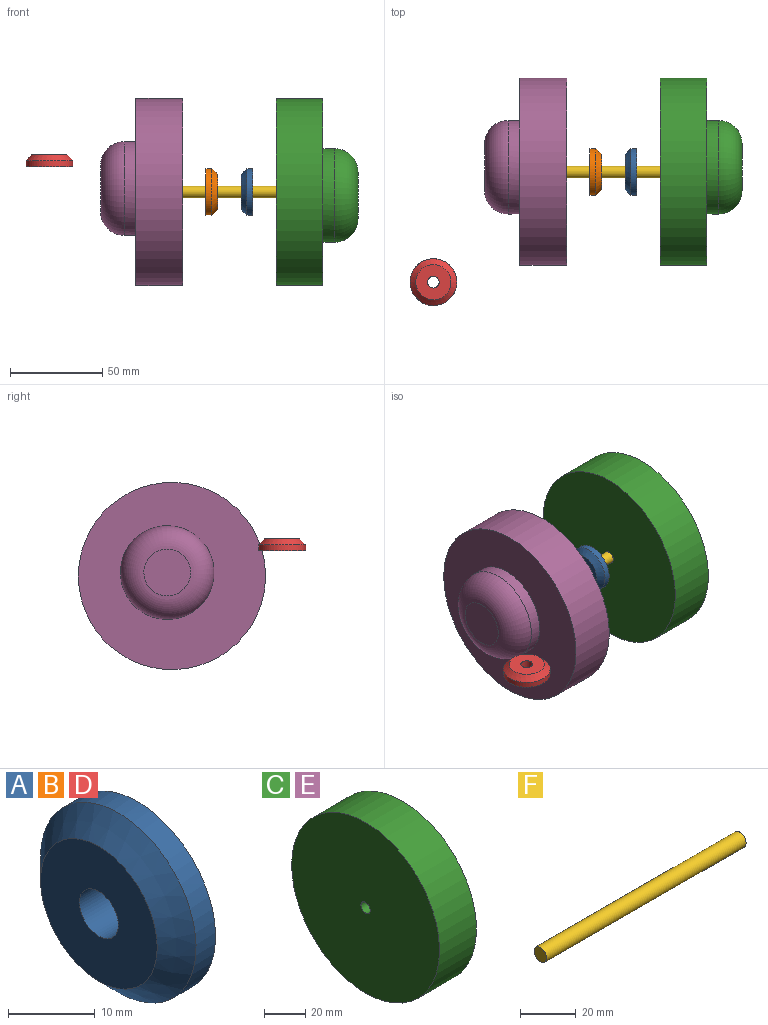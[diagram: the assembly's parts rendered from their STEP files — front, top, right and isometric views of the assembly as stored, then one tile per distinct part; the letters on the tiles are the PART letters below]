
ASSEMBLY  parts=6 mates=4
PART A: 5 faces, bbox 6.4x25.4x25.4 mm
  f0: cylinder r=12.7mm len=25.4mm, axis (1,0,0), area 253.4mm2, adj f2,f4
  f1: plane 19.05x19.05mm, normal (-1,0,0), area 253.4mm2, adj f3,f4
  f2: plane 25.4x25.4mm, normal (1,0,0), area 475mm2, adj f0,f3
  f3: cylinder r=3.17mm len=6.35mm, axis (1,0,0), area 126.7mm2, adj f1,f2
  f4: cone r=12.7mm half-angle=45deg, axis (1,0,0), area 313.5mm2, adj f0,f1
PART B: same geometry as A
PART C: 8 faces, bbox 44.5x101.6x101.6 mm
  f0: cylinder r=50.8mm len=101.6mm, axis (-1,0,0), area 8107.3mm2, adj f1,f2
  f1: plane 101.6x101.6mm, normal (1,0,0), area 6080.5mm2, adj f0,f5
  f2: plane 101.6x101.6mm, normal (-1,0,0), area 8075.7mm2, adj f0,f3
  f3: cylinder r=3.17mm len=25.4mm, axis (1,0,0), area 506.7mm2, adj f2,f6
  f4: plane 25.4x25.4mm, normal (1,0,0), area 506.7mm2, adj f7
  f5: cylinder r=25.4mm len=50.8mm, axis (-1,0,0), area 1013.4mm2, adj f1,f7
  f6: plane 6.35x6.35mm, normal (-1,0,0), area 31.7mm2, adj f3
  f7: torus R=12.7mm, axis (1,0,0), area 2605.3mm2, adj f4,f5
PART D: same geometry as A
PART E: same geometry as C
PART F: 3 faces, bbox 101.6x6.4x6.4 mm
  f0: cylinder r=3.17mm len=101.6mm, axis (-1,0,0), area 2026.8mm2, adj f1,f2
  f1: plane 6.35x6.35mm, normal (1,0,0), area 31.7mm2, adj f0
  f2: plane 6.35x6.35mm, normal (-1,0,0), area 31.7mm2, adj f0
PLACE A t=(50.12,49.85,20.24)mm
PLACE B rot(axis=(0,1,0),180deg) t=(24.72,49.85,20.24)mm
PLACE C t=(62.82,49.85,20.24)mm
PLACE D rot(axis=(0,1,0),90deg) t=(-60.29,-9.99,34.04)mm
PLACE E rot(axis=(0,1,0),180deg) t=(12.02,49.85,20.24)mm
PLACE F t=(-13.38,49.85,20.54)mm
MATE revolute B.f0 <-> F.f0  axis (1,0,0) through (31.07,49.85,20.24)mm
MATE revolute A.f0 <-> F.f0  axis (1,0,0) through (50.12,49.85,20.24)mm
MATE fastened F.f0 <-> C.f0  axis (-1,0,0) through (88.22,49.85,20.24)mm
MATE fastened E.f0 <-> F.f0  axis (-1,0,0) through (-13.38,49.85,20.24)mm
